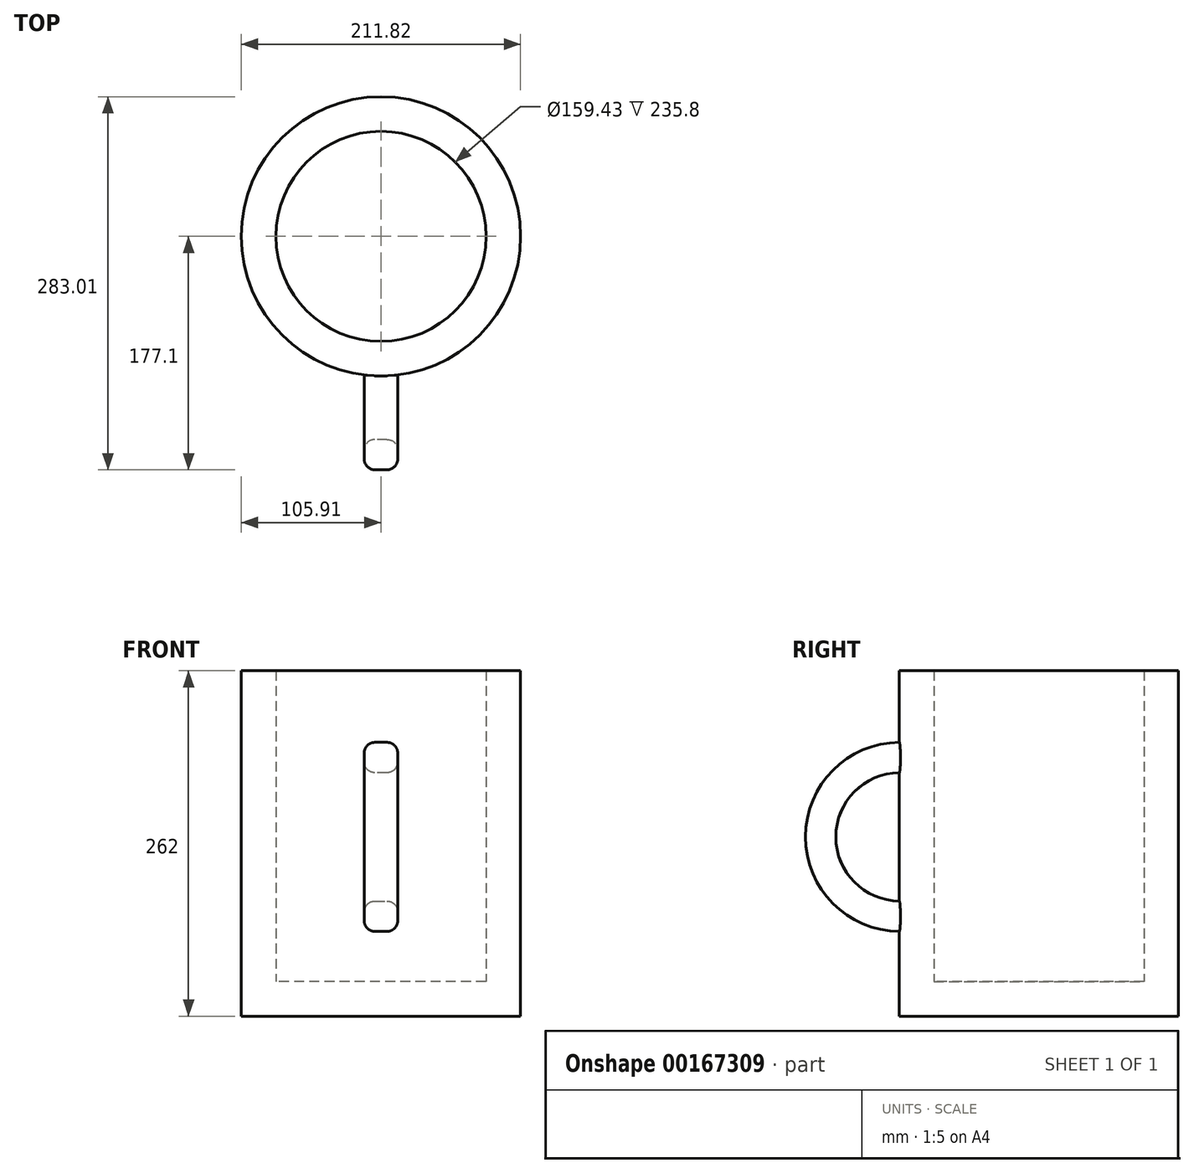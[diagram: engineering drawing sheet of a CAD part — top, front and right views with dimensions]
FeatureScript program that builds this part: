
annotation { "Feature Type Name" : "Feature", "Feature Type Description" : "" }
export const myFeature = defineFeature(function(context is Context, id is Id, definition is map)
    precondition{}
    {
        {
            var Q0;
            Q0=qCreatedBy(makeId("Top.planeOp"),FACE);
            var sketch = newSketch(context, id + "F0", { "sketchPlane" : qUnion([Q0])});
            skCircle(sketch, "E0", {"center": v(0, 0) * mm, "radius": 105.91 * mm});
            skSolve(sketch);
        }
        {
            var Q0;
            Q0=makeQuery(id+"F0.imprint","IMPRINT",FACE,{"disambiguationData":[TD([[makeQuery(id+"F0.imprint","IMPRINT",EDGE,{"derivedFrom":sQuery(id+"F0.wireOp",EDGE,"E0")}),1.0]])]});
            extrude(context, id + "F1", {"entities" : qUnion([Q0]), "depth" : 262 * mm});
        }
        {
            var Q0;
            Q0=qCreatedBy(makeId("Right.planeOp"),FACE);
            var sketch = newSketch(context, id + "F2", { "sketchPlane" : qUnion([Q0])});
            skCircle(sketch, "E1", {"center": v(-105.37, 136) * mm, "radius": 71.74 * mm});
            skCircle(sketch, "E2", {"center": v(-105.37, 136) * mm, "radius": 48.7 * mm});
            skSolve(sketch);
        }
        {
            var Q0;
            Q0 = qSketchRegion(id + "F2", true);
            extrude(context, id + "F3", {"entities" : qUnion([Q0]), "operationType" : NewBodyOperationType.ADD, "endBound" : BoundingType.SYMMETRIC, "depth" : 25.4 * mm});
        }
        {
            var Q0;
            Q0=makeQuery(id+"F3.opExtrude","CAP_EDGE",EDGE,{"disambiguationData":[OSD([sQuery(id+"F2.wireOp",EDGE,"E1")])],"isStart":true});
            var Q1;
            Q1=makeQuery(id+"F3.opExtrude","CAP_EDGE",EDGE,{"disambiguationData":[OSD([sQuery(id+"F2.wireOp",EDGE,"E1")])],"isStart":false});
            var Q2;
            Q2=makeQuery(id+"F3.opExtrude","CAP_EDGE",EDGE,{"disambiguationData":[OSD([sQuery(id+"F2.wireOp",EDGE,"E2")])],"isStart":true});
            var Q3;
            Q3=makeQuery(id+"F3.opExtrude","CAP_EDGE",EDGE,{"disambiguationData":[OSD([sQuery(id+"F2.wireOp",EDGE,"E2")])],"isStart":false});
            fillet(context, id + "F4", {"entities" : qUnion([Q0, Q1, Q2, Q3]), "radius" : 8.13 * mm, "tangentPropagation" : true, "allowEdgeOverflow" : false});
        }
        {
            var Q0;
            Q0=makeQuery(id+"F1.opExtrude","CAP_FACE",FACE,{"disambiguationData":[OSD([sQuery(id+"F0.wireOp",EDGE,"E0")])],"isStart":false});
            shell(context, id + "F5", {"entities" : qUnion([Q0]), "thickness" : 26.2 * mm});
        }
    });
